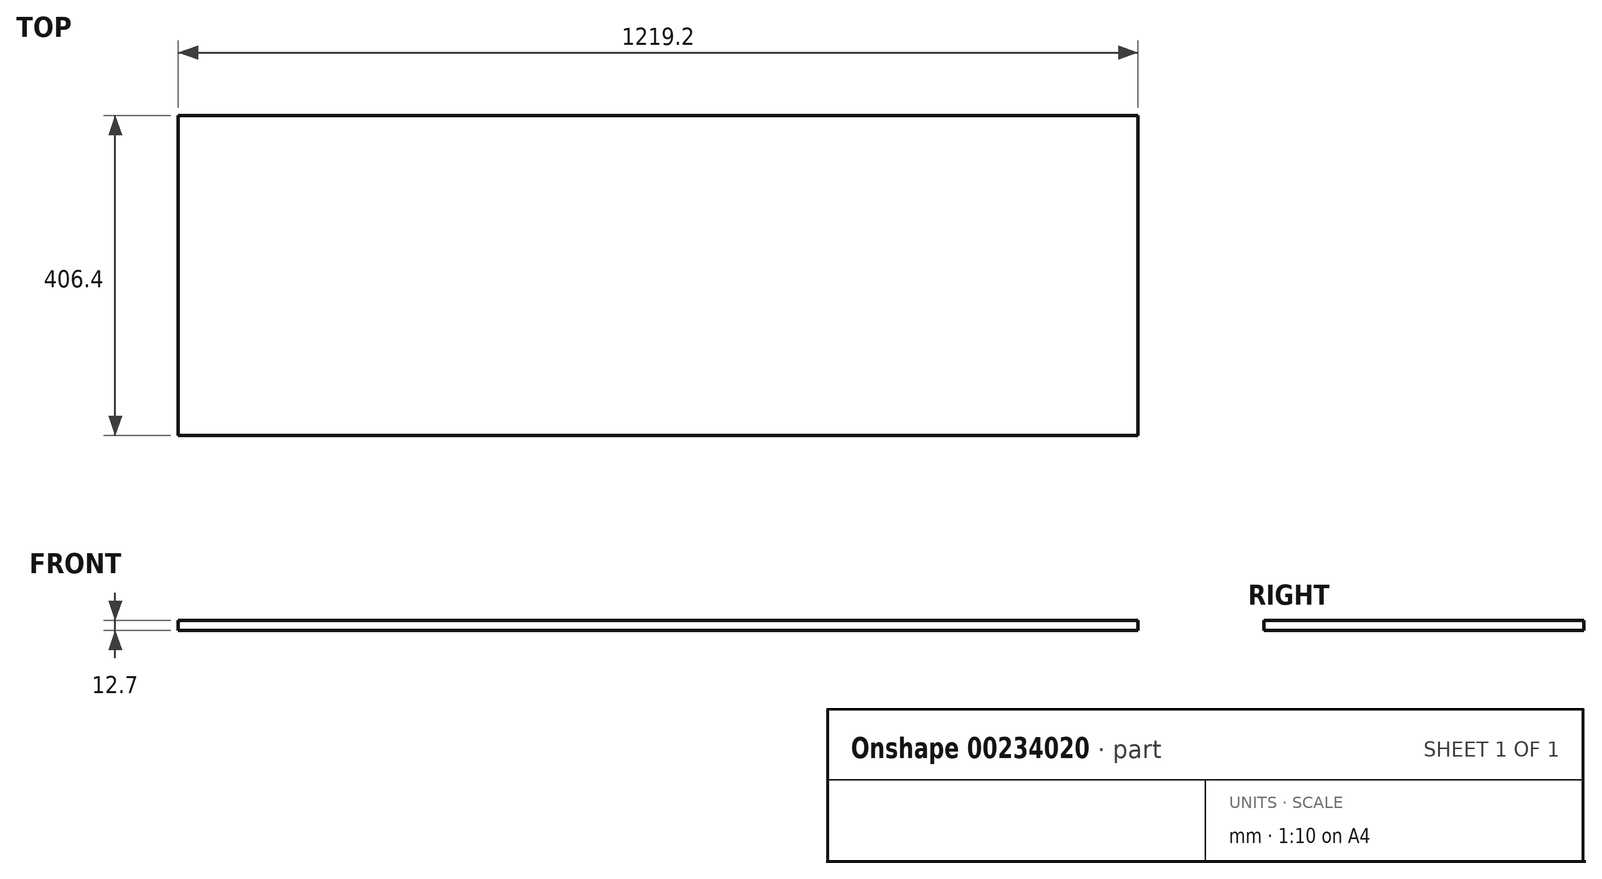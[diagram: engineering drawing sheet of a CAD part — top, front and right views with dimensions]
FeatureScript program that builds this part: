
annotation { "Feature Type Name" : "Feature", "Feature Type Description" : "" }
export const myFeature = defineFeature(function(context is Context, id is Id, definition is map)
    precondition{}
    {
        {
            var Q0;
            Q0=qCreatedBy(makeId("Top.planeOp"),FACE);
            var sketch = newSketch(context, id + "F0", { "sketchPlane" : qUnion([Q0])});
            skLineSegment(sketch, "E0.bottom", {"start": v(-604.13, 112.78) * mm, "end": v(615.07, 112.78) * mm});
            skLineSegment(sketch, "E0.top", {"start": v(-604.13, -293.62) * mm, "end": v(615.07, -293.62) * mm});
            skLineSegment(sketch, "E0.left", {"start": v(-604.13, 112.78) * mm, "end": v(-604.13, -293.62) * mm});
            skLineSegment(sketch, "E0.right", {"start": v(615.07, 112.78) * mm, "end": v(615.07, -293.62) * mm});
            skSolve(sketch);
        }
        {
            var Q0;
            Q0 = qSketchRegion(id + "F0", true);
            extrude(context, id + "F1", {"entities" : qUnion([Q0]), "depth" : 12.7 * mm});
        }
    });
